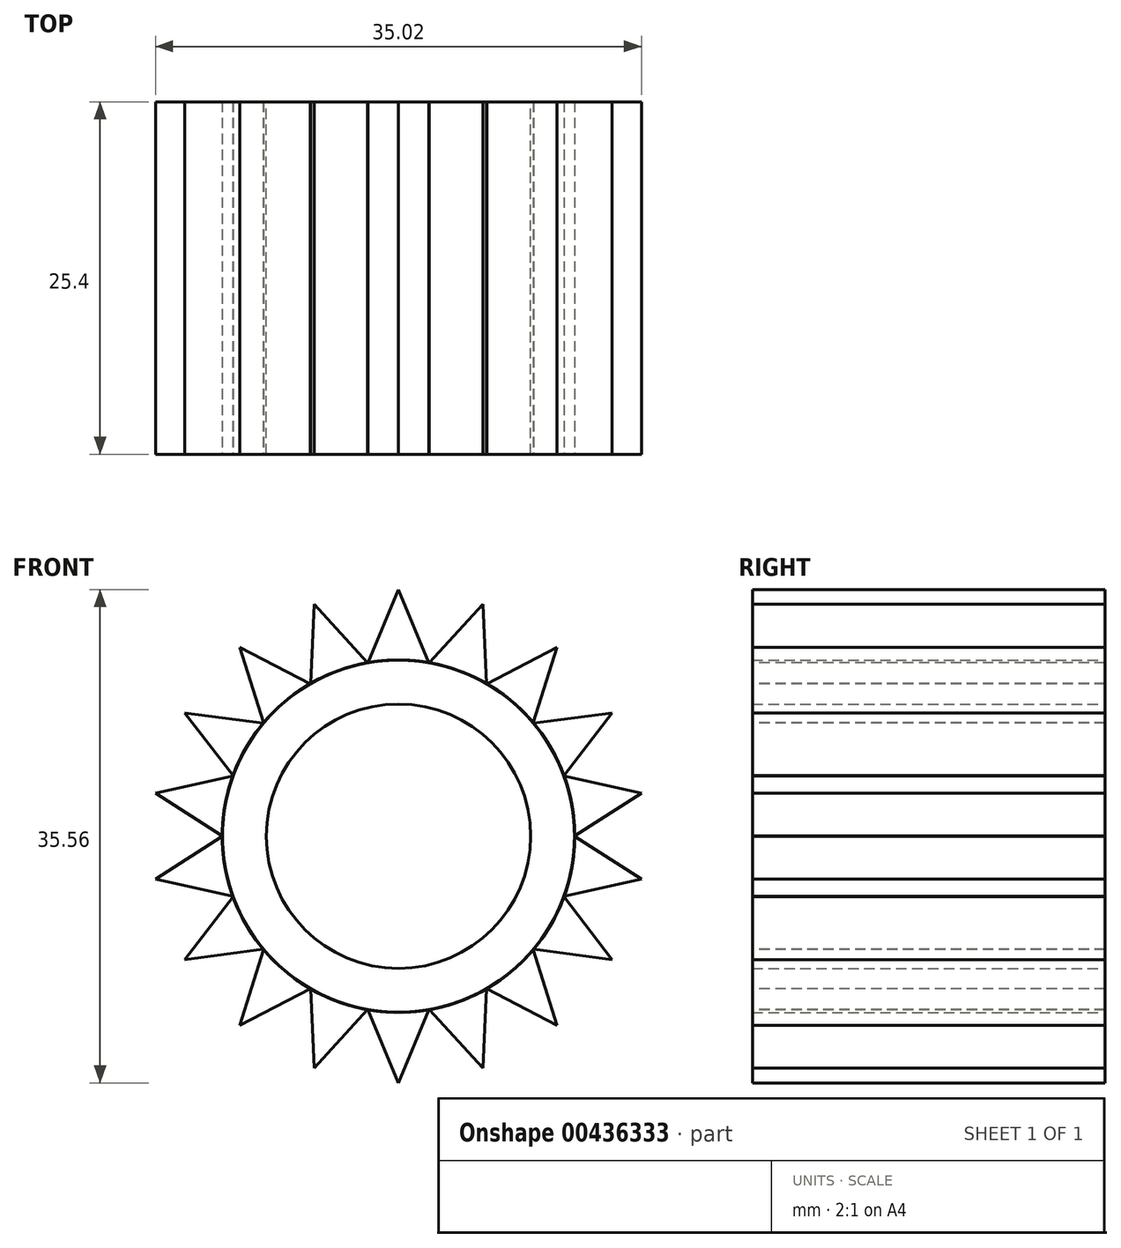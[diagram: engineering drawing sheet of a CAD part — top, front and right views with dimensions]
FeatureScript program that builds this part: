
annotation { "Feature Type Name" : "Feature", "Feature Type Description" : "" }
export const myFeature = defineFeature(function(context is Context, id is Id, definition is map)
    precondition{}
    {
        {
            var Q0;
            Q0=qCreatedBy(makeId("Front.planeOp"),FACE);
            var sketch = newSketch(context, id + "F0", { "sketchPlane" : qUnion([Q0])});
            skCircle(sketch, "E0", {"center": v(0, 0) * mm, "radius": 12.7 * mm});
            skCircle(sketch, "E1", {"center": v(0, 0) * mm, "radius": 9.53 * mm});
            skSolve(sketch);
        }
        {
            var Q0;
            Q0 = qSketchRegion(id + "F0", true);
            extrude(context, id + "F1", {"entities" : qUnion([Q0]), "endBound" : BoundingType.SYMMETRIC, "depth" : 25.4 * mm});
        }
        {
            var Q0;
            Q0=makeQuery(id+"F1.opExtrude","CAP_FACE",FACE,{"disambiguationData":[OSD([sQuery(id+"F0.wireOp",EDGE,"E0"),sQuery(id+"F0.wireOp",EDGE,"E1")])],"isStart":false});
            var sketch = newSketch(context, id + "F2", { "sketchPlane" : qUnion([Q0])});
            skLineSegment(sketch, "E2", {"start": v(0, 12.7) * mm, "end": v(0, 17.78) * mm});
            skLineSegment(sketch, "E3", {"start": v(0, 17.78) * mm, "end": v(-2.18, 12.51) * mm});
            skLineSegment(sketch, "E4", {"start": v(-2.18, 12.51) * mm, "end": v(2.18, 12.51) * mm});
            skLineSegment(sketch, "E5", {"start": v(2.18, 12.51) * mm, "end": v(0, 17.78) * mm});
            skSolve(sketch);
        }
        {
            var Q0;
            Q0 = qSketchRegion(id + "F2", true);
            extrude(context, id + "F3", {"entities" : qUnion([Q0]), "operationType" : NewBodyOperationType.ADD, "oppositeDirection" : true, "depth" : 25.4 * mm});
        }
        {
            var Q0;
            Q0=qCreatedBy(makeId("Right.planeOp"),FACE);
            var sketch = newSketch(context, id + "F4", { "sketchPlane" : qUnion([Q0])});
            skLineSegment(sketch, "E6", {"start": v(27.01, 0) * mm, "end": v(-24.5, 0) * mm});
            skSolve(sketch);
        }
        {
            var Q0;
            Q0=makeQuery(id+"F1.opExtrude","SWEPT_BODY",BODY,{"disambiguationData":[OSD([sQuery(id+"F0.wireOp",EDGE,"E0"),sQuery(id+"F0.wireOp",EDGE,"E1")])]});
            var Q1;
            Q1=sQuery(id+"F4.wireOp",EDGE,"E6");
            circularPattern(context, id + "F5", {"entities" : qUnion([Q0]), "axis" : qUnion([Q1]), "angle" : 360 * degree, "instanceCount" : 18, "equalSpace" : true});
        }
    });
